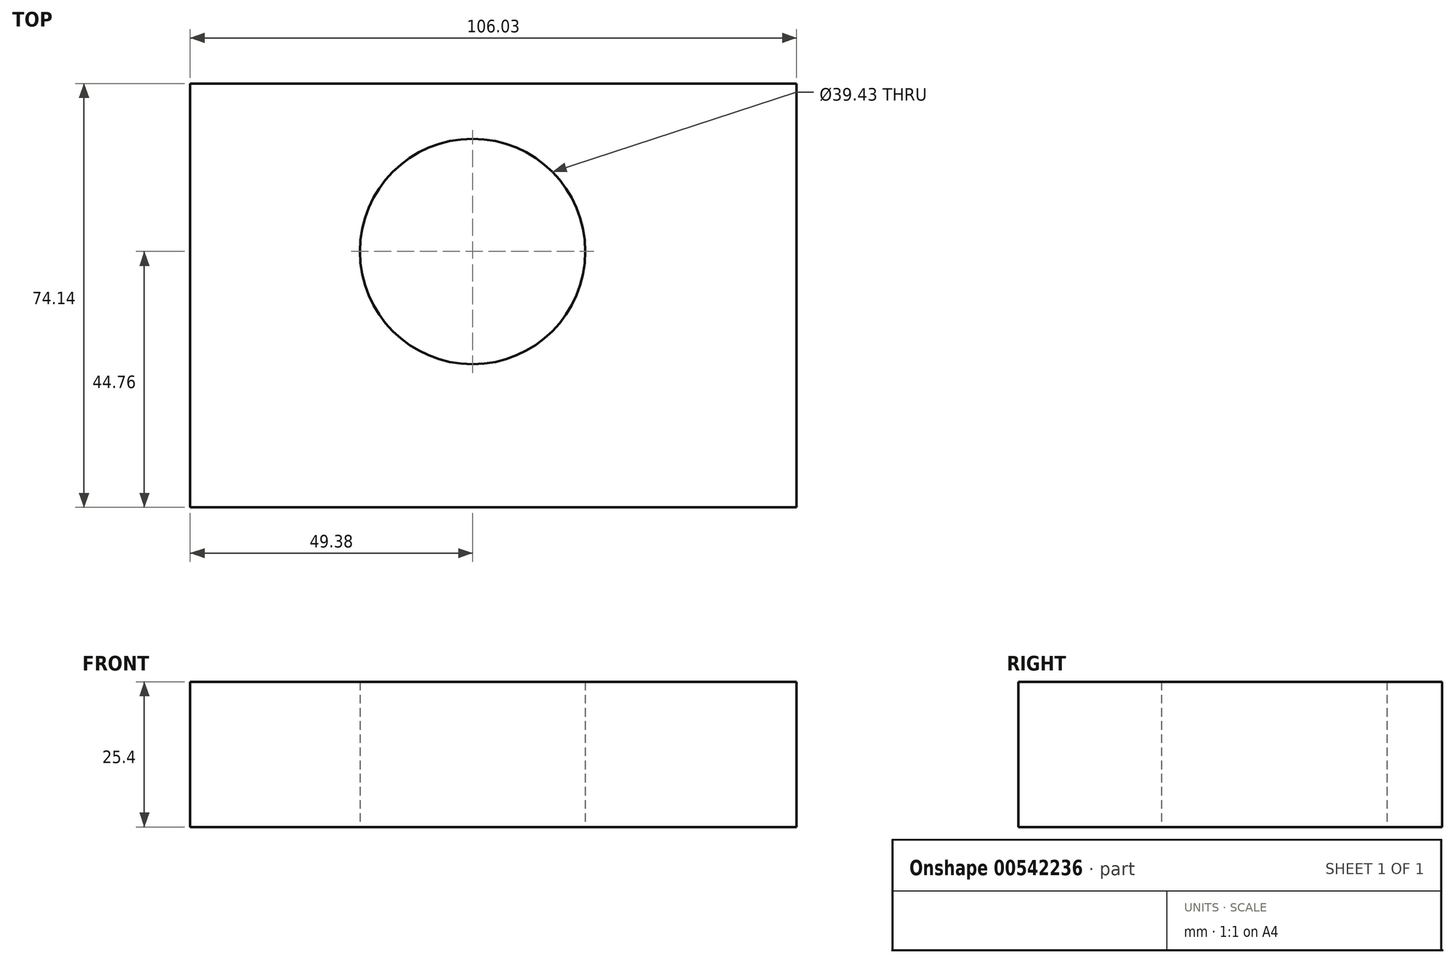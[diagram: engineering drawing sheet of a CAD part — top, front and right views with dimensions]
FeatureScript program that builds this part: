
annotation { "Feature Type Name" : "Feature", "Feature Type Description" : "" }
export const myFeature = defineFeature(function(context is Context, id is Id, definition is map)
    precondition{}
    {
        {
            var Q0;
            Q0=qCreatedBy(makeId("Top.planeOp"),FACE);
            var sketch = newSketch(context, id + "F0", { "sketchPlane" : qUnion([Q0])});
            skLineSegment(sketch, "E0.bottom", {"start": v(-49.38, 29.38) * mm, "end": v(56.65, 29.38) * mm});
            skLineSegment(sketch, "E0.top", {"start": v(-49.38, -44.76) * mm, "end": v(56.65, -44.76) * mm});
            skLineSegment(sketch, "E0.left", {"start": v(-49.38, 29.38) * mm, "end": v(-49.38, -44.76) * mm});
            skLineSegment(sketch, "E0.right", {"start": v(56.65, 29.38) * mm, "end": v(56.65, -44.76) * mm});
            skCircle(sketch, "E1", {"center": v(0, 0) * mm, "radius": 19.71 * mm});
            skSolve(sketch);
        }
        {
            var Q0;
            Q0 = qSketchRegion(id + "F0", true);
            extrude(context, id + "F1", {"entities" : qUnion([Q0]), "depth" : 25.4 * mm, "offsetDistance" : 25.4 * mm});
        }
    });
